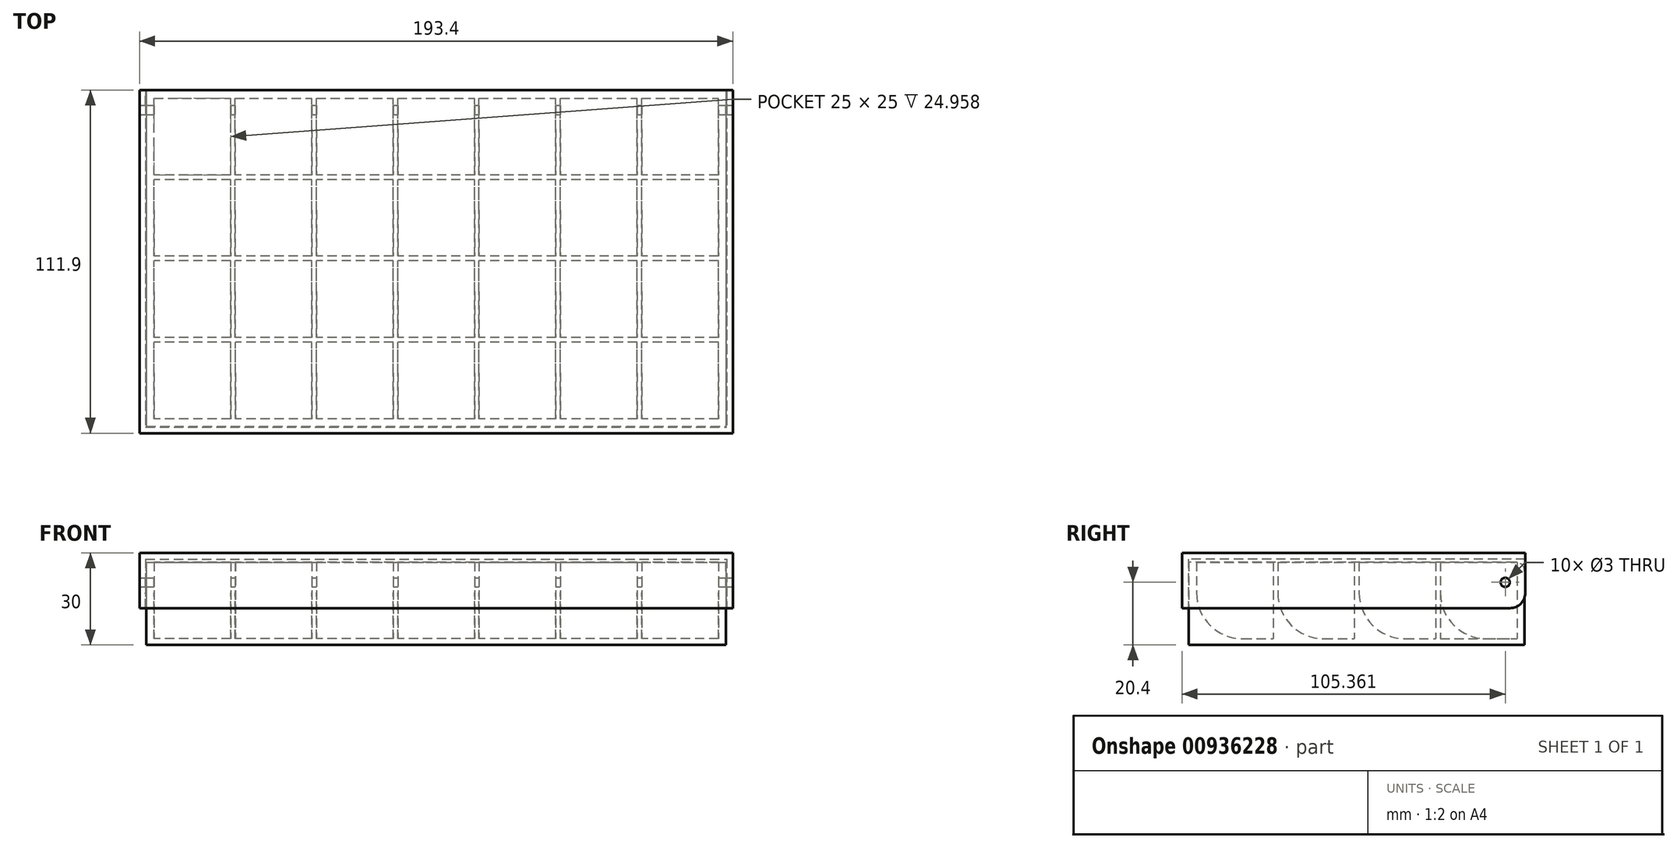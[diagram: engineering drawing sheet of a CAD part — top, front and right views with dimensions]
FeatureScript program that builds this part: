
annotation { "Feature Type Name" : "Feature", "Feature Type Description" : "" }
export const myFeature = defineFeature(function(context is Context, id is Id, definition is map)
    precondition{}
    {
        {
            var Q0;
            Q0=qCreatedBy(makeId("Top.planeOp"),FACE);
            var sketch = newSketch(context, id + "F0", { "sketchPlane" : qUnion([Q0])});
            skLineSegment(sketch, "E0.bottom", {"start": v(12.5, -12.5) * mm, "end": v(-12.5, -12.5) * mm});
            skLineSegment(sketch, "E0.top", {"start": v(12.5, 12.5) * mm, "end": v(-12.5, 12.5) * mm});
            skLineSegment(sketch, "E0.left", {"start": v(12.5, -12.5) * mm, "end": v(12.5, 12.5) * mm});
            skLineSegment(sketch, "E0.right", {"start": v(-12.5, -12.5) * mm, "end": v(-12.5, 12.5) * mm});
            skPoint(sketch, "E0.middle", {"position": v(0, 0) * mm});
            skLineSegment(sketch, "E1.1.0.0", {"start": v(39, -12.5) * mm, "end": v(39, 12.5) * mm});
            skLineSegment(sketch, "E1.1.0.1", {"start": v(14, -12.5) * mm, "end": v(14, 12.5) * mm});
            skLineSegment(sketch, "E1.1.0.2", {"start": v(39, 12.5) * mm, "end": v(14, 12.5) * mm});
            skLineSegment(sketch, "E1.1.0.3", {"start": v(39, -12.5) * mm, "end": v(14, -12.5) * mm});
            skLineSegment(sketch, "E1.2.0.0", {"start": v(65.5, -12.5) * mm, "end": v(65.5, 12.5) * mm});
            skLineSegment(sketch, "E1.2.0.1", {"start": v(40.5, -12.5) * mm, "end": v(40.5, 12.5) * mm});
            skLineSegment(sketch, "E1.2.0.2", {"start": v(65.5, 12.5) * mm, "end": v(40.5, 12.5) * mm});
            skLineSegment(sketch, "E1.2.0.3", {"start": v(65.5, -12.5) * mm, "end": v(40.5, -12.5) * mm});
            skLineSegment(sketch, "E1.direction1", {"start": v(12.5, -12.5) * mm, "end": v(39, -12.5) * mm, "construction": true});
            skLineSegment(sketch, "E2.0.3.0", {"start": v(92, -12.5) * mm, "end": v(92, 12.5) * mm});
            skLineSegment(sketch, "E2.3.3.0", {"start": v(67, -12.5) * mm, "end": v(67, 12.5) * mm});
            skLineSegment(sketch, "E2.6.3.0", {"start": v(92, 12.5) * mm, "end": v(67, 12.5) * mm});
            skLineSegment(sketch, "E2.9.3.0", {"start": v(92, -12.5) * mm, "end": v(67, -12.5) * mm});
            skLineSegment(sketch, "E2.0.4.0", {"start": v(118.5, -12.5) * mm, "end": v(118.5, 12.5) * mm});
            skLineSegment(sketch, "E2.3.4.0", {"start": v(93.5, -12.5) * mm, "end": v(93.5, 12.5) * mm});
            skLineSegment(sketch, "E2.6.4.0", {"start": v(118.5, 12.5) * mm, "end": v(93.5, 12.5) * mm});
            skLineSegment(sketch, "E2.9.4.0", {"start": v(118.5, -12.5) * mm, "end": v(93.5, -12.5) * mm});
            skLineSegment(sketch, "E2.0.5.0", {"start": v(145, -12.5) * mm, "end": v(145, 12.5) * mm});
            skLineSegment(sketch, "E2.3.5.0", {"start": v(120, -12.5) * mm, "end": v(120, 12.5) * mm});
            skLineSegment(sketch, "E2.6.5.0", {"start": v(145, 12.5) * mm, "end": v(120, 12.5) * mm});
            skLineSegment(sketch, "E2.9.5.0", {"start": v(145, -12.5) * mm, "end": v(120, -12.5) * mm});
            skLineSegment(sketch, "E2.0.6.0", {"start": v(171.5, -12.5) * mm, "end": v(171.5, 12.5) * mm});
            skLineSegment(sketch, "E2.3.6.0", {"start": v(146.5, -12.5) * mm, "end": v(146.5, 12.5) * mm});
            skLineSegment(sketch, "E2.6.6.0", {"start": v(171.5, 12.5) * mm, "end": v(146.5, 12.5) * mm});
            skLineSegment(sketch, "E2.9.6.0", {"start": v(171.5, -12.5) * mm, "end": v(146.5, -12.5) * mm});
            skLineSegment(sketch, "E3.bottom", {"start": v(12.5, -39) * mm, "end": v(-12.5, -39) * mm});
            skLineSegment(sketch, "E3.top", {"start": v(12.5, -14) * mm, "end": v(-12.5, -14) * mm});
            skLineSegment(sketch, "E3.left", {"start": v(12.5, -39) * mm, "end": v(12.5, -14) * mm});
            skLineSegment(sketch, "E3.right", {"start": v(-12.5, -39) * mm, "end": v(-12.5, -14) * mm});
            skPoint(sketch, "E3.middle", {"position": v(0, -26.5) * mm});
            skLineSegment(sketch, "E4.1.0.0", {"start": v(39, -39) * mm, "end": v(39, -14) * mm});
            skLineSegment(sketch, "E4.1.0.1", {"start": v(14, -39) * mm, "end": v(14, -14) * mm});
            skLineSegment(sketch, "E4.1.0.2", {"start": v(39, -14) * mm, "end": v(14, -14) * mm});
            skLineSegment(sketch, "E4.1.0.3", {"start": v(39, -39) * mm, "end": v(14, -39) * mm});
            skLineSegment(sketch, "E4.2.0.0", {"start": v(65.5, -39) * mm, "end": v(65.5, -14) * mm});
            skLineSegment(sketch, "E4.2.0.1", {"start": v(40.5, -39) * mm, "end": v(40.5, -14) * mm});
            skLineSegment(sketch, "E4.2.0.2", {"start": v(65.5, -14) * mm, "end": v(40.5, -14) * mm});
            skLineSegment(sketch, "E4.2.0.3", {"start": v(65.5, -39) * mm, "end": v(40.5, -39) * mm});
            skLineSegment(sketch, "E4.direction1", {"start": v(12.5, -39) * mm, "end": v(39, -39) * mm, "construction": true});
            skLineSegment(sketch, "E5.0.3.0", {"start": v(92, -39) * mm, "end": v(92, -14) * mm});
            skLineSegment(sketch, "E5.3.3.0", {"start": v(67, -39) * mm, "end": v(67, -14) * mm});
            skLineSegment(sketch, "E5.6.3.0", {"start": v(92, -14) * mm, "end": v(67, -14) * mm});
            skLineSegment(sketch, "E5.9.3.0", {"start": v(92, -39) * mm, "end": v(67, -39) * mm});
            skLineSegment(sketch, "E5.0.4.0", {"start": v(118.5, -39) * mm, "end": v(118.5, -14) * mm});
            skLineSegment(sketch, "E5.3.4.0", {"start": v(93.5, -39) * mm, "end": v(93.5, -14) * mm});
            skLineSegment(sketch, "E5.6.4.0", {"start": v(118.5, -14) * mm, "end": v(93.5, -14) * mm});
            skLineSegment(sketch, "E5.9.4.0", {"start": v(118.5, -39) * mm, "end": v(93.5, -39) * mm});
            skLineSegment(sketch, "E5.0.5.0", {"start": v(145, -39) * mm, "end": v(145, -14) * mm});
            skLineSegment(sketch, "E5.3.5.0", {"start": v(120, -39) * mm, "end": v(120, -14) * mm});
            skLineSegment(sketch, "E5.6.5.0", {"start": v(145, -14) * mm, "end": v(120, -14) * mm});
            skLineSegment(sketch, "E5.9.5.0", {"start": v(145, -39) * mm, "end": v(120, -39) * mm});
            skLineSegment(sketch, "E5.0.6.0", {"start": v(171.5, -39) * mm, "end": v(171.5, -14) * mm});
            skLineSegment(sketch, "E5.3.6.0", {"start": v(146.5, -39) * mm, "end": v(146.5, -14) * mm});
            skLineSegment(sketch, "E5.6.6.0", {"start": v(171.5, -14) * mm, "end": v(146.5, -14) * mm});
            skLineSegment(sketch, "E5.9.6.0", {"start": v(171.5, -39) * mm, "end": v(146.5, -39) * mm});
            skLineSegment(sketch, "E6.bottom", {"start": v(12.5, -65.5) * mm, "end": v(-12.5, -65.5) * mm});
            skLineSegment(sketch, "E6.top", {"start": v(12.5, -40.5) * mm, "end": v(-12.5, -40.5) * mm});
            skLineSegment(sketch, "E6.left", {"start": v(12.5, -65.5) * mm, "end": v(12.5, -40.5) * mm});
            skLineSegment(sketch, "E6.right", {"start": v(-12.5, -65.5) * mm, "end": v(-12.5, -40.5) * mm});
            skPoint(sketch, "E6.middle", {"position": v(0, -53) * mm});
            skLineSegment(sketch, "E7.1.0.0", {"start": v(39, -65.5) * mm, "end": v(39, -40.5) * mm});
            skLineSegment(sketch, "E7.1.0.1", {"start": v(14, -65.5) * mm, "end": v(14, -40.5) * mm});
            skLineSegment(sketch, "E7.1.0.2", {"start": v(39, -40.5) * mm, "end": v(14, -40.5) * mm});
            skLineSegment(sketch, "E7.1.0.3", {"start": v(39, -65.5) * mm, "end": v(14, -65.5) * mm});
            skLineSegment(sketch, "E7.2.0.0", {"start": v(65.5, -65.5) * mm, "end": v(65.5, -40.5) * mm});
            skLineSegment(sketch, "E7.2.0.1", {"start": v(40.5, -65.5) * mm, "end": v(40.5, -40.5) * mm});
            skLineSegment(sketch, "E7.2.0.2", {"start": v(65.5, -40.5) * mm, "end": v(40.5, -40.5) * mm});
            skLineSegment(sketch, "E7.2.0.3", {"start": v(65.5, -65.5) * mm, "end": v(40.5, -65.5) * mm});
            skLineSegment(sketch, "E7.direction1", {"start": v(12.5, -65.5) * mm, "end": v(39, -65.5) * mm, "construction": true});
            skLineSegment(sketch, "E8.0.3.0", {"start": v(92, -65.5) * mm, "end": v(92, -40.5) * mm});
            skLineSegment(sketch, "E8.3.3.0", {"start": v(67, -65.5) * mm, "end": v(67, -40.5) * mm});
            skLineSegment(sketch, "E8.6.3.0", {"start": v(92, -40.5) * mm, "end": v(67, -40.5) * mm});
            skLineSegment(sketch, "E8.9.3.0", {"start": v(92, -65.5) * mm, "end": v(67, -65.5) * mm});
            skLineSegment(sketch, "E8.0.4.0", {"start": v(118.5, -65.5) * mm, "end": v(118.5, -40.5) * mm});
            skLineSegment(sketch, "E8.3.4.0", {"start": v(93.5, -65.5) * mm, "end": v(93.5, -40.5) * mm});
            skLineSegment(sketch, "E8.6.4.0", {"start": v(118.5, -40.5) * mm, "end": v(93.5, -40.5) * mm});
            skLineSegment(sketch, "E8.9.4.0", {"start": v(118.5, -65.5) * mm, "end": v(93.5, -65.5) * mm});
            skLineSegment(sketch, "E8.0.5.0", {"start": v(145, -65.5) * mm, "end": v(145, -40.5) * mm});
            skLineSegment(sketch, "E8.3.5.0", {"start": v(120, -65.5) * mm, "end": v(120, -40.5) * mm});
            skLineSegment(sketch, "E8.6.5.0", {"start": v(145, -40.5) * mm, "end": v(120, -40.5) * mm});
            skLineSegment(sketch, "E8.9.5.0", {"start": v(145, -65.5) * mm, "end": v(120, -65.5) * mm});
            skLineSegment(sketch, "E8.0.6.0", {"start": v(171.5, -65.5) * mm, "end": v(171.5, -40.5) * mm});
            skLineSegment(sketch, "E8.3.6.0", {"start": v(146.5, -65.5) * mm, "end": v(146.5, -40.5) * mm});
            skLineSegment(sketch, "E8.6.6.0", {"start": v(171.5, -40.5) * mm, "end": v(146.5, -40.5) * mm});
            skLineSegment(sketch, "E8.9.6.0", {"start": v(171.5, -65.5) * mm, "end": v(146.5, -65.5) * mm});
            skLineSegment(sketch, "E9.bottom", {"start": v(12.52, -92) * mm, "end": v(-12.48, -92) * mm});
            skLineSegment(sketch, "E9.top", {"start": v(12.52, -67) * mm, "end": v(-12.48, -67) * mm});
            skLineSegment(sketch, "E9.left", {"start": v(12.52, -92) * mm, "end": v(12.52, -67) * mm});
            skLineSegment(sketch, "E9.right", {"start": v(-12.48, -92) * mm, "end": v(-12.48, -67) * mm});
            skPoint(sketch, "E9.middle", {"position": v(0.02, -79.5) * mm});
            skLineSegment(sketch, "E10.1.0.0", {"start": v(39.02, -92) * mm, "end": v(39.02, -67) * mm});
            skLineSegment(sketch, "E10.1.0.1", {"start": v(14.02, -92) * mm, "end": v(14.02, -67) * mm});
            skLineSegment(sketch, "E10.1.0.2", {"start": v(39.02, -67) * mm, "end": v(14.02, -67) * mm});
            skLineSegment(sketch, "E10.1.0.3", {"start": v(39.02, -92) * mm, "end": v(14.02, -92) * mm});
            skLineSegment(sketch, "E10.2.0.0", {"start": v(65.52, -92) * mm, "end": v(65.52, -67) * mm});
            skLineSegment(sketch, "E10.2.0.1", {"start": v(40.52, -92) * mm, "end": v(40.52, -67) * mm});
            skLineSegment(sketch, "E10.2.0.2", {"start": v(65.52, -67) * mm, "end": v(40.52, -67) * mm});
            skLineSegment(sketch, "E10.2.0.3", {"start": v(65.52, -92) * mm, "end": v(40.52, -92) * mm});
            skLineSegment(sketch, "E10.direction1", {"start": v(12.52, -92) * mm, "end": v(39.02, -92) * mm, "construction": true});
            skLineSegment(sketch, "E11.0.3.0", {"start": v(92.02, -92) * mm, "end": v(92.02, -67) * mm});
            skLineSegment(sketch, "E11.3.3.0", {"start": v(67.02, -92) * mm, "end": v(67.02, -67) * mm});
            skLineSegment(sketch, "E11.6.3.0", {"start": v(92.02, -67) * mm, "end": v(67.02, -67) * mm});
            skLineSegment(sketch, "E11.9.3.0", {"start": v(92.02, -92) * mm, "end": v(67.02, -92) * mm});
            skLineSegment(sketch, "E11.0.4.0", {"start": v(118.52, -92) * mm, "end": v(118.52, -67) * mm});
            skLineSegment(sketch, "E11.3.4.0", {"start": v(93.52, -92) * mm, "end": v(93.52, -67) * mm});
            skLineSegment(sketch, "E11.6.4.0", {"start": v(118.52, -67) * mm, "end": v(93.52, -67) * mm});
            skLineSegment(sketch, "E11.9.4.0", {"start": v(118.52, -92) * mm, "end": v(93.52, -92) * mm});
            skLineSegment(sketch, "E11.0.5.0", {"start": v(145.02, -92) * mm, "end": v(145.02, -67) * mm});
            skLineSegment(sketch, "E11.3.5.0", {"start": v(120.02, -92) * mm, "end": v(120.02, -67) * mm});
            skLineSegment(sketch, "E11.6.5.0", {"start": v(145.02, -67) * mm, "end": v(120.02, -67) * mm});
            skLineSegment(sketch, "E11.9.5.0", {"start": v(145.02, -92) * mm, "end": v(120.02, -92) * mm});
            skLineSegment(sketch, "E11.0.6.0", {"start": v(171.52, -92) * mm, "end": v(171.52, -67) * mm});
            skLineSegment(sketch, "E11.3.6.0", {"start": v(146.52, -92) * mm, "end": v(146.52, -67) * mm});
            skLineSegment(sketch, "E11.6.6.0", {"start": v(171.52, -67) * mm, "end": v(146.52, -67) * mm});
            skLineSegment(sketch, "E11.9.6.0", {"start": v(171.52, -92) * mm, "end": v(146.52, -92) * mm});
            skLineSegment(sketch, "E12.bottom", {"start": v(-15, 15) * mm, "end": v(174, 15) * mm});
            skLineSegment(sketch, "E12.top", {"start": v(-15, -94.5) * mm, "end": v(174, -94.5) * mm});
            skLineSegment(sketch, "E12.left", {"start": v(-15, 15) * mm, "end": v(-15, -94.5) * mm});
            skLineSegment(sketch, "E12.right", {"start": v(174, 15) * mm, "end": v(174, -94.5) * mm});
            skSolve(sketch);
        }
        {
            var Q0;
            Q0=makeQuery(id+"F0.imprint","IMPRINT",FACE,{"disambiguationData":[TD([[makeQuery(id+"F0.imprint","IMPRINT",EDGE,{"derivedFrom":sQuery(id+"F0.wireOp",EDGE,"E0.bottom")}),1.0]])]});
            extrude(context, id + "F1", {"entities" : qUnion([Q0]), "depth" : 25 * mm, "offsetDistance" : 25 * mm});
        }
        {
            var Q0;
            Q0=qCreatedBy(makeId("Top.planeOp"),FACE);
            var sketch = newSketch(context, id + "F2", { "sketchPlane" : qUnion([Q0])});
            skLineSegment(sketch, "E13.0", {"start": v(-15, 15) * mm, "end": v(174, 15) * mm});
            skLineSegment(sketch, "E13.1", {"start": v(-15, 15) * mm, "end": v(-15, -94.5) * mm});
            skLineSegment(sketch, "E13.2", {"start": v(-15, -94.5) * mm, "end": v(174, -94.5) * mm});
            skLineSegment(sketch, "E13.3", {"start": v(174, 15) * mm, "end": v(174, -94.5) * mm});
            skSolve(sketch);
        }
        {
            var Q0;
            Q0 = qSketchRegion(id + "F2", true);
            extrude(context, id + "F3", {"entities" : qUnion([Q0]), "operationType" : NewBodyOperationType.ADD, "oppositeDirection" : true, "depth" : 2 * mm, "offsetDistance" : 25 * mm});
        }
        {
            var Q0;
            Q0=makeQuery(id+"F1.opExtrude","CAP_EDGE",EDGE,{"disambiguationData":[OSD([sQuery(id+"F0.wireOp",EDGE,"E0.bottom")])],"isStart":true});
            var Q1;
            Q1=makeQuery(id+"F1.opExtrude","CAP_EDGE",EDGE,{"disambiguationData":[OSD([sQuery(id+"F0.wireOp",EDGE,"E1.1.0.3")])],"isStart":true});
            var Q2;
            Q2=makeQuery(id+"F1.opExtrude","CAP_EDGE",EDGE,{"disambiguationData":[OSD([sQuery(id+"F0.wireOp",EDGE,"E1.2.0.3")])],"isStart":true});
            var Q3;
            Q3=makeQuery(id+"F1.opExtrude","CAP_EDGE",EDGE,{"disambiguationData":[OSD([sQuery(id+"F0.wireOp",EDGE,"E2.9.3.0")])],"isStart":true});
            var Q4;
            Q4=makeQuery(id+"F1.opExtrude","CAP_EDGE",EDGE,{"disambiguationData":[OSD([sQuery(id+"F0.wireOp",EDGE,"E2.9.4.0")])],"isStart":true});
            var Q5;
            Q5=makeQuery(id+"F1.opExtrude","CAP_EDGE",EDGE,{"disambiguationData":[OSD([sQuery(id+"F0.wireOp",EDGE,"E2.9.5.0")])],"isStart":true});
            var Q6;
            Q6=makeQuery(id+"F1.opExtrude","CAP_EDGE",EDGE,{"disambiguationData":[OSD([sQuery(id+"F0.wireOp",EDGE,"E2.9.6.0")])],"isStart":true});
            var Q7;
            Q7=makeQuery(id+"F1.opExtrude","CAP_EDGE",EDGE,{"disambiguationData":[OSD([sQuery(id+"F0.wireOp",EDGE,"E3.bottom")])],"isStart":true});
            var Q8;
            Q8=makeQuery(id+"F1.opExtrude","CAP_EDGE",EDGE,{"disambiguationData":[OSD([sQuery(id+"F0.wireOp",EDGE,"E4.1.0.3")])],"isStart":true});
            var Q9;
            Q9=makeQuery(id+"F1.opExtrude","CAP_EDGE",EDGE,{"disambiguationData":[OSD([sQuery(id+"F0.wireOp",EDGE,"E4.2.0.3")])],"isStart":true});
            var Q10;
            Q10=makeQuery(id+"F1.opExtrude","CAP_EDGE",EDGE,{"disambiguationData":[OSD([sQuery(id+"F0.wireOp",EDGE,"E5.9.3.0")])],"isStart":true});
            var Q11;
            Q11=makeQuery(id+"F1.opExtrude","CAP_EDGE",EDGE,{"disambiguationData":[OSD([sQuery(id+"F0.wireOp",EDGE,"E5.9.4.0")])],"isStart":true});
            var Q12;
            Q12=makeQuery(id+"F1.opExtrude","CAP_EDGE",EDGE,{"disambiguationData":[OSD([sQuery(id+"F0.wireOp",EDGE,"E5.9.5.0")])],"isStart":true});
            var Q13;
            Q13=makeQuery(id+"F1.opExtrude","CAP_EDGE",EDGE,{"disambiguationData":[OSD([sQuery(id+"F0.wireOp",EDGE,"E5.9.6.0")])],"isStart":true});
            var Q14;
            Q14=makeQuery(id+"F1.opExtrude","CAP_EDGE",EDGE,{"disambiguationData":[OSD([sQuery(id+"F0.wireOp",EDGE,"E8.9.6.0")])],"isStart":true});
            var Q15;
            Q15=makeQuery(id+"F1.opExtrude","CAP_EDGE",EDGE,{"disambiguationData":[OSD([sQuery(id+"F0.wireOp",EDGE,"E8.9.5.0")])],"isStart":true});
            var Q16;
            Q16=makeQuery(id+"F1.opExtrude","CAP_EDGE",EDGE,{"disambiguationData":[OSD([sQuery(id+"F0.wireOp",EDGE,"E8.9.4.0")])],"isStart":true});
            var Q17;
            Q17=makeQuery(id+"F1.opExtrude","CAP_EDGE",EDGE,{"disambiguationData":[OSD([sQuery(id+"F0.wireOp",EDGE,"E8.9.3.0")])],"isStart":true});
            var Q18;
            Q18=makeQuery(id+"F1.opExtrude","CAP_EDGE",EDGE,{"disambiguationData":[OSD([sQuery(id+"F0.wireOp",EDGE,"E7.2.0.3")])],"isStart":true});
            var Q19;
            Q19=makeQuery(id+"F1.opExtrude","CAP_EDGE",EDGE,{"disambiguationData":[OSD([sQuery(id+"F0.wireOp",EDGE,"E7.1.0.3")])],"isStart":true});
            var Q20;
            Q20=makeQuery(id+"F1.opExtrude","CAP_EDGE",EDGE,{"disambiguationData":[OSD([sQuery(id+"F0.wireOp",EDGE,"E6.bottom")])],"isStart":true});
            var Q21;
            Q21=makeQuery(id+"F1.opExtrude","CAP_EDGE",EDGE,{"disambiguationData":[OSD([sQuery(id+"F0.wireOp",EDGE,"E9.bottom")])],"isStart":true});
            var Q22;
            Q22=makeQuery(id+"F1.opExtrude","CAP_EDGE",EDGE,{"disambiguationData":[OSD([sQuery(id+"F0.wireOp",EDGE,"E10.1.0.3")])],"isStart":true});
            var Q23;
            Q23=makeQuery(id+"F1.opExtrude","CAP_EDGE",EDGE,{"disambiguationData":[OSD([sQuery(id+"F0.wireOp",EDGE,"E10.2.0.3")])],"isStart":true});
            var Q24;
            Q24=makeQuery(id+"F1.opExtrude","CAP_EDGE",EDGE,{"disambiguationData":[OSD([sQuery(id+"F0.wireOp",EDGE,"E11.9.3.0")])],"isStart":true});
            var Q25;
            Q25=makeQuery(id+"F1.opExtrude","CAP_EDGE",EDGE,{"disambiguationData":[OSD([sQuery(id+"F0.wireOp",EDGE,"E11.9.4.0")])],"isStart":true});
            var Q26;
            Q26=makeQuery(id+"F1.opExtrude","CAP_EDGE",EDGE,{"disambiguationData":[OSD([sQuery(id+"F0.wireOp",EDGE,"E11.9.5.0")])],"isStart":true});
            var Q27;
            Q27=makeQuery(id+"F1.opExtrude","CAP_EDGE",EDGE,{"disambiguationData":[OSD([sQuery(id+"F0.wireOp",EDGE,"E11.9.6.0")])],"isStart":true});
            fillet(context, id + "F4", {"entities" : qUnion([Q0, Q1, Q2, Q3, Q4, Q5, Q6, Q7, Q8, Q9, Q10, Q11, Q12, Q13, Q14, Q15, Q16, Q17, Q18, Q19, Q20, Q21, Q22, Q23, Q24, Q25, Q26, Q27]), "radius" : 15 * mm, "tangentPropagation" : true, "allowEdgeOverflow" : false});
        }
        {
            var Q0;
            Q0=makeQuery(id+"F1.opExtrude","CAP_FACE",FACE,{"disambiguationData":[OSD([sQuery(id+"F0.wireOp",EDGE,"E0.bottom"),sQuery(id+"F0.wireOp",EDGE,"E0.top"),sQuery(id+"F0.wireOp",EDGE,"E0.left"),sQuery(id+"F0.wireOp",EDGE,"E0.right"),sQuery(id+"F0.wireOp",EDGE,"E1.1.0.0"),sQuery(id+"F0.wireOp",EDGE,"E1.1.0.1"),sQuery(id+"F0.wireOp",EDGE,"E1.1.0.2"),sQuery(id+"F0.wireOp",EDGE,"E1.1.0.3"),sQuery(id+"F0.wireOp",EDGE,"E1.2.0.0"),sQuery(id+"F0.wireOp",EDGE,"E1.2.0.1"),sQuery(id+"F0.wireOp",EDGE,"E1.2.0.2"),sQuery(id+"F0.wireOp",EDGE,"E1.2.0.3"),sQuery(id+"F0.wireOp",EDGE,"E2.0.3.0"),sQuery(id+"F0.wireOp",EDGE,"E2.3.3.0"),sQuery(id+"F0.wireOp",EDGE,"E2.6.3.0"),sQuery(id+"F0.wireOp",EDGE,"E2.9.3.0"),sQuery(id+"F0.wireOp",EDGE,"E2.0.4.0"),sQuery(id+"F0.wireOp",EDGE,"E2.3.4.0"),sQuery(id+"F0.wireOp",EDGE,"E2.6.4.0"),sQuery(id+"F0.wireOp",EDGE,"E2.9.4.0"),sQuery(id+"F0.wireOp",EDGE,"E2.0.5.0"),sQuery(id+"F0.wireOp",EDGE,"E2.3.5.0"),sQuery(id+"F0.wireOp",EDGE,"E2.6.5.0"),sQuery(id+"F0.wireOp",EDGE,"E2.9.5.0"),sQuery(id+"F0.wireOp",EDGE,"E2.0.6.0"),sQuery(id+"F0.wireOp",EDGE,"E2.3.6.0"),sQuery(id+"F0.wireOp",EDGE,"E2.6.6.0"),sQuery(id+"F0.wireOp",EDGE,"E2.9.6.0"),sQuery(id+"F0.wireOp",EDGE,"E3.bottom"),sQuery(id+"F0.wireOp",EDGE,"E3.top"),sQuery(id+"F0.wireOp",EDGE,"E3.left"),sQuery(id+"F0.wireOp",EDGE,"E3.right"),sQuery(id+"F0.wireOp",EDGE,"E4.1.0.0"),sQuery(id+"F0.wireOp",EDGE,"E4.1.0.1"),sQuery(id+"F0.wireOp",EDGE,"E4.1.0.2"),sQuery(id+"F0.wireOp",EDGE,"E4.1.0.3"),sQuery(id+"F0.wireOp",EDGE,"E4.2.0.0"),sQuery(id+"F0.wireOp",EDGE,"E4.2.0.1"),sQuery(id+"F0.wireOp",EDGE,"E4.2.0.2"),sQuery(id+"F0.wireOp",EDGE,"E4.2.0.3"),sQuery(id+"F0.wireOp",EDGE,"E5.0.3.0"),sQuery(id+"F0.wireOp",EDGE,"E5.3.3.0"),sQuery(id+"F0.wireOp",EDGE,"E5.6.3.0"),sQuery(id+"F0.wireOp",EDGE,"E5.9.3.0"),sQuery(id+"F0.wireOp",EDGE,"E5.0.4.0"),sQuery(id+"F0.wireOp",EDGE,"E5.3.4.0"),sQuery(id+"F0.wireOp",EDGE,"E5.6.4.0"),sQuery(id+"F0.wireOp",EDGE,"E5.9.4.0"),sQuery(id+"F0.wireOp",EDGE,"E5.0.5.0"),sQuery(id+"F0.wireOp",EDGE,"E5.3.5.0"),sQuery(id+"F0.wireOp",EDGE,"E5.6.5.0"),sQuery(id+"F0.wireOp",EDGE,"E5.9.5.0"),sQuery(id+"F0.wireOp",EDGE,"E5.0.6.0"),sQuery(id+"F0.wireOp",EDGE,"E5.3.6.0"),sQuery(id+"F0.wireOp",EDGE,"E5.6.6.0"),sQuery(id+"F0.wireOp",EDGE,"E5.9.6.0"),sQuery(id+"F0.wireOp",EDGE,"E6.bottom"),sQuery(id+"F0.wireOp",EDGE,"E6.top"),sQuery(id+"F0.wireOp",EDGE,"E6.left"),sQuery(id+"F0.wireOp",EDGE,"E6.right"),sQuery(id+"F0.wireOp",EDGE,"E7.1.0.0"),sQuery(id+"F0.wireOp",EDGE,"E7.1.0.1"),sQuery(id+"F0.wireOp",EDGE,"E7.1.0.2"),sQuery(id+"F0.wireOp",EDGE,"E7.1.0.3"),sQuery(id+"F0.wireOp",EDGE,"E7.2.0.0"),sQuery(id+"F0.wireOp",EDGE,"E7.2.0.1"),sQuery(id+"F0.wireOp",EDGE,"E7.2.0.2"),sQuery(id+"F0.wireOp",EDGE,"E7.2.0.3"),sQuery(id+"F0.wireOp",EDGE,"E8.0.3.0"),sQuery(id+"F0.wireOp",EDGE,"E8.3.3.0"),sQuery(id+"F0.wireOp",EDGE,"E8.6.3.0"),sQuery(id+"F0.wireOp",EDGE,"E8.9.3.0"),sQuery(id+"F0.wireOp",EDGE,"E8.0.4.0"),sQuery(id+"F0.wireOp",EDGE,"E8.3.4.0"),sQuery(id+"F0.wireOp",EDGE,"E8.6.4.0"),sQuery(id+"F0.wireOp",EDGE,"E8.9.4.0"),sQuery(id+"F0.wireOp",EDGE,"E8.0.5.0"),sQuery(id+"F0.wireOp",EDGE,"E8.3.5.0"),sQuery(id+"F0.wireOp",EDGE,"E8.6.5.0"),sQuery(id+"F0.wireOp",EDGE,"E8.9.5.0"),sQuery(id+"F0.wireOp",EDGE,"E8.0.6.0"),sQuery(id+"F0.wireOp",EDGE,"E8.3.6.0"),sQuery(id+"F0.wireOp",EDGE,"E8.6.6.0"),sQuery(id+"F0.wireOp",EDGE,"E8.9.6.0"),sQuery(id+"F0.wireOp",EDGE,"E9.bottom"),sQuery(id+"F0.wireOp",EDGE,"E9.top"),sQuery(id+"F0.wireOp",EDGE,"E9.left"),sQuery(id+"F0.wireOp",EDGE,"E9.right"),sQuery(id+"F0.wireOp",EDGE,"E10.1.0.0"),sQuery(id+"F0.wireOp",EDGE,"E10.1.0.1"),sQuery(id+"F0.wireOp",EDGE,"E10.1.0.2"),sQuery(id+"F0.wireOp",EDGE,"E10.1.0.3"),sQuery(id+"F0.wireOp",EDGE,"E10.2.0.0"),sQuery(id+"F0.wireOp",EDGE,"E10.2.0.1"),sQuery(id+"F0.wireOp",EDGE,"E10.2.0.2"),sQuery(id+"F0.wireOp",EDGE,"E10.2.0.3"),sQuery(id+"F0.wireOp",EDGE,"E11.0.3.0"),sQuery(id+"F0.wireOp",EDGE,"E11.3.3.0"),sQuery(id+"F0.wireOp",EDGE,"E11.6.3.0"),sQuery(id+"F0.wireOp",EDGE,"E11.9.3.0"),sQuery(id+"F0.wireOp",EDGE,"E11.0.4.0"),sQuery(id+"F0.wireOp",EDGE,"E11.3.4.0"),sQuery(id+"F0.wireOp",EDGE,"E11.6.4.0"),sQuery(id+"F0.wireOp",EDGE,"E11.9.4.0"),sQuery(id+"F0.wireOp",EDGE,"E11.0.5.0"),sQuery(id+"F0.wireOp",EDGE,"E11.3.5.0"),sQuery(id+"F0.wireOp",EDGE,"E11.6.5.0"),sQuery(id+"F0.wireOp",EDGE,"E11.9.5.0"),sQuery(id+"F0.wireOp",EDGE,"E11.0.6.0"),sQuery(id+"F0.wireOp",EDGE,"E11.3.6.0"),sQuery(id+"F0.wireOp",EDGE,"E11.6.6.0"),sQuery(id+"F0.wireOp",EDGE,"E11.9.6.0"),sQuery(id+"F0.wireOp",EDGE,"E12.bottom"),sQuery(id+"F0.wireOp",EDGE,"E12.top"),sQuery(id+"F0.wireOp",EDGE,"E12.left"),sQuery(id+"F0.wireOp",EDGE,"E12.right")])],"isStart":false});
            var sketch = newSketch(context, id + "F5", { "sketchPlane" : qUnion([Q0])});
            skLineSegment(sketch, "E14.1", {"start": v(-15.2, 15.2) * mm, "end": v(-15.2, -94.7) * mm});
            skLineSegment(sketch, "E14.2", {"start": v(-15.2, -94.7) * mm, "end": v(174.2, -94.7) * mm});
            skLineSegment(sketch, "E14.3", {"start": v(174.2, 15.2) * mm, "end": v(174.2, -94.7) * mm});
            skLineSegment(sketch, "E15.0", {"start": v(-17.2, 15.2) * mm, "end": v(-15.2, 15.2) * mm});
            skLineSegment(sketch, "E15.1", {"start": v(-17.2, 15.2) * mm, "end": v(-17.2, -96.7) * mm});
            skLineSegment(sketch, "E15.2", {"start": v(-17.2, -96.7) * mm, "end": v(176.2, -96.7) * mm});
            skLineSegment(sketch, "E15.3", {"start": v(176.2, 15.2) * mm, "end": v(176.2, -96.7) * mm});
            skLineSegment(sketch, "E16", {"start": v(-15.2, 15.2) * mm, "end": v(-15.2, 15.2) * mm});
            skLineSegment(sketch, "E17", {"start": v(174.2, 15.2) * mm, "end": v(174.2, 15.2) * mm});
            skLineSegment(sketch, "E18.trimOffspring", {"start": v(174.2, 15.2) * mm, "end": v(176.2, 15.2) * mm});
            skSolve(sketch);
        }
        {
            var Q0;
            Q0 = qSketchRegion(id + "F5", true);
            extrude(context, id + "F6", {"entities" : qUnion([Q0]), "depth" : 3 * mm, "offsetDistance" : 25 * mm, "hasSecondDirection" : true, "secondDirectionOppositeDirection" : true, "secondDirectionDepth" : 15 * mm});
        }
        {
            var Q0;
            Q0=makeQuery(id+"F6.opExtrude","CAP_FACE",FACE,{"disambiguationData":[OSD([sQuery(id+"F5.wireOp",EDGE,"E14.0"),sQuery(id+"F5.wireOp",EDGE,"E14.1"),sQuery(id+"F5.wireOp",EDGE,"E14.2"),sQuery(id+"F5.wireOp",EDGE,"E14.3"),sQuery(id+"F5.wireOp",EDGE,"E15.0"),sQuery(id+"F5.wireOp",EDGE,"E15.1"),sQuery(id+"F5.wireOp",EDGE,"E15.2"),sQuery(id+"F5.wireOp",EDGE,"E15.3")])],"isStart":false});
            var sketch = newSketch(context, id + "F7", { "sketchPlane" : qUnion([Q0])});
            skLineSegment(sketch, "E19.0", {"start": v(-17.2, 15.2) * mm, "end": v(176.2, 15.2) * mm});
            skLineSegment(sketch, "E19.1", {"start": v(-17.2, 15.2) * mm, "end": v(-17.2, -96.7) * mm});
            skLineSegment(sketch, "E19.2", {"start": v(-17.2, -96.7) * mm, "end": v(176.2, -96.7) * mm});
            skLineSegment(sketch, "E19.3", {"start": v(176.2, 15.2) * mm, "end": v(176.2, -96.7) * mm});
            skSolve(sketch);
        }
        {
            var Q0;
            Q0 = qSketchRegion(id + "F7", true);
            extrude(context, id + "F8", {"entities" : qUnion([Q0]), "operationType" : NewBodyOperationType.ADD, "oppositeDirection" : true, "depth" : 2 * mm, "offsetDistance" : 25 * mm});
        }
        {
            var Q0;
            Q0=makeQuery(id+"F1.opExtrude","CAP_EDGE",EDGE,{"disambiguationData":[OSD([sQuery(id+"F0.wireOp",EDGE,"E12.bottom")])],"isStart":false});
            fillet(context, id + "F9", {"entities" : qUnion([Q0]), "radius" : 3 * mm, "tangentPropagation" : true, "allowEdgeOverflow" : false});
        }
        {
            var Q0;
            Q0=makeQuery(id+"F6.opExtrude","SWEPT_FACE",FACE,{"disambiguationData":[OSD([sQuery(id+"F5.wireOp",EDGE,"E15.3")])]});
            var sketch = newSketch(context, id + "F10", { "sketchPlane" : qUnion([Q0])});
            skCircle(sketch, "E20", {"center": v(8.66, 18.4) * mm, "radius": 1.5 * mm});
            skSolve(sketch);
        }
        {
            var Q0;
            Q0=makeQuery(id+"F10.imprint","IMPRINT",FACE,{"disambiguationData":[TD([[makeQuery(id+"F10.imprint","IMPRINT",EDGE,{"derivedFrom":sQuery(id+"F10.wireOp",EDGE,"E20")}),1.0]])]});
            extrude(context, id + "F11", {"entities" : qUnion([Q0]), "operationType" : NewBodyOperationType.REMOVE, "oppositeDirection" : true, "depth" : 200 * mm, "offsetDistance" : 25 * mm});
        }
        {
            var Q0;
            Q0=makeQuery(id+"F6.opExtrude","CAP_EDGE",EDGE,{"disambiguationData":[OSD([sQuery(id+"F5.wireOp",EDGE,"E18.trimOffspring")])],"isStart":true});
            var Q1;
            Q1=makeQuery(id+"F6.opExtrude","CAP_EDGE",EDGE,{"disambiguationData":[OSD([sQuery(id+"F5.wireOp",EDGE,"E15.0")])],"isStart":true});
            fillet(context, id + "F12", {"entities" : qUnion([Q0, Q1]), "radius" : 5 * mm, "tangentPropagation" : true, "allowEdgeOverflow" : false});
        }
    });
